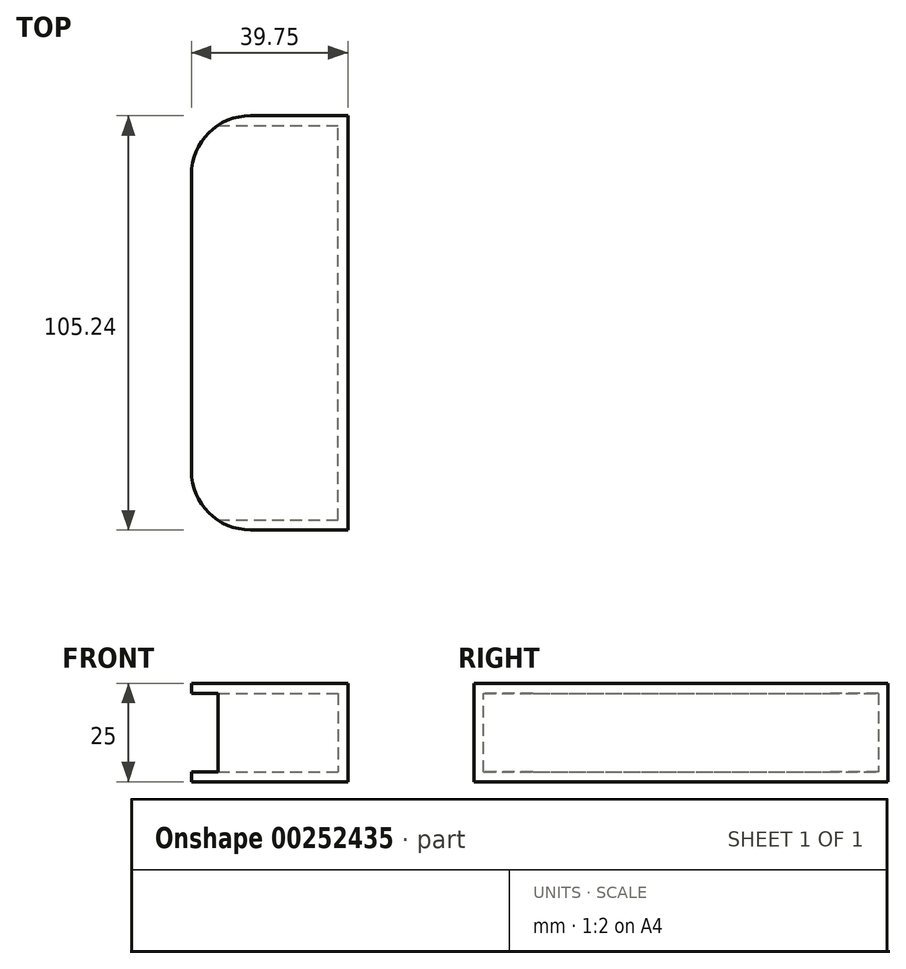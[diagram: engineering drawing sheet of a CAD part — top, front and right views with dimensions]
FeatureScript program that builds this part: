
annotation { "Feature Type Name" : "Feature", "Feature Type Description" : "" }
export const myFeature = defineFeature(function(context is Context, id is Id, definition is map)
    precondition{}
    {
        {
            var Q0;
            Q0=qCreatedBy(makeId("Top.planeOp"),FACE);
            var sketch = newSketch(context, id + "F0", { "sketchPlane" : qUnion([Q0])});
            skLineSegment(sketch, "E0.bottom", {"start": v(-18.29, -30.6) * mm, "end": v(21.46, -30.6) * mm});
            skLineSegment(sketch, "E0.top", {"start": v(-18.29, 74.64) * mm, "end": v(21.46, 74.64) * mm});
            skLineSegment(sketch, "E0.left", {"start": v(-18.29, -30.6) * mm, "end": v(-18.29, 74.64) * mm});
            skLineSegment(sketch, "E0.right", {"start": v(21.46, -30.6) * mm, "end": v(21.46, 74.64) * mm});
            skSolve(sketch);
        }
        {
            var Q0;
            Q0 = qSketchRegion(id + "F0", true);
            extrude(context, id + "F1", {"entities" : qUnion([Q0]), "depth" : 25 * mm});
        }
        {
            var Q0;
            Q0=makeQuery(id+"F1.opExtrude","SWEPT_FACE",FACE,{"disambiguationData":[OSD([sQuery(id+"F0.wireOp",EDGE,"E0.left")])]});
            shell(context, id + "F2", {"entities" : qUnion([Q0]), "thickness" : 2.5 * mm});
        }
        {
            var Q0;
            Q0=makeQuery(id+"F1.opExtrude","SWEPT_EDGE",EDGE,{"disambiguationData":[OSD([sQuery(id+"F0.wireOp",EDGE,"E0.top"),sQuery(id+"F0.wireOp",EDGE,"E0.left")])]});
            var Q1;
            Q1=makeQuery(id+"F1.opExtrude","SWEPT_EDGE",EDGE,{"disambiguationData":[OSD([sQuery(id+"F0.wireOp",EDGE,"E0.bottom"),sQuery(id+"F0.wireOp",EDGE,"E0.left")])]});
            fillet(context, id + "F3", {"entities" : qUnion([Q0, Q1]), "radius" : 15 * mm, "tangentPropagation" : true, "allowEdgeOverflow" : false});
        }
    });
